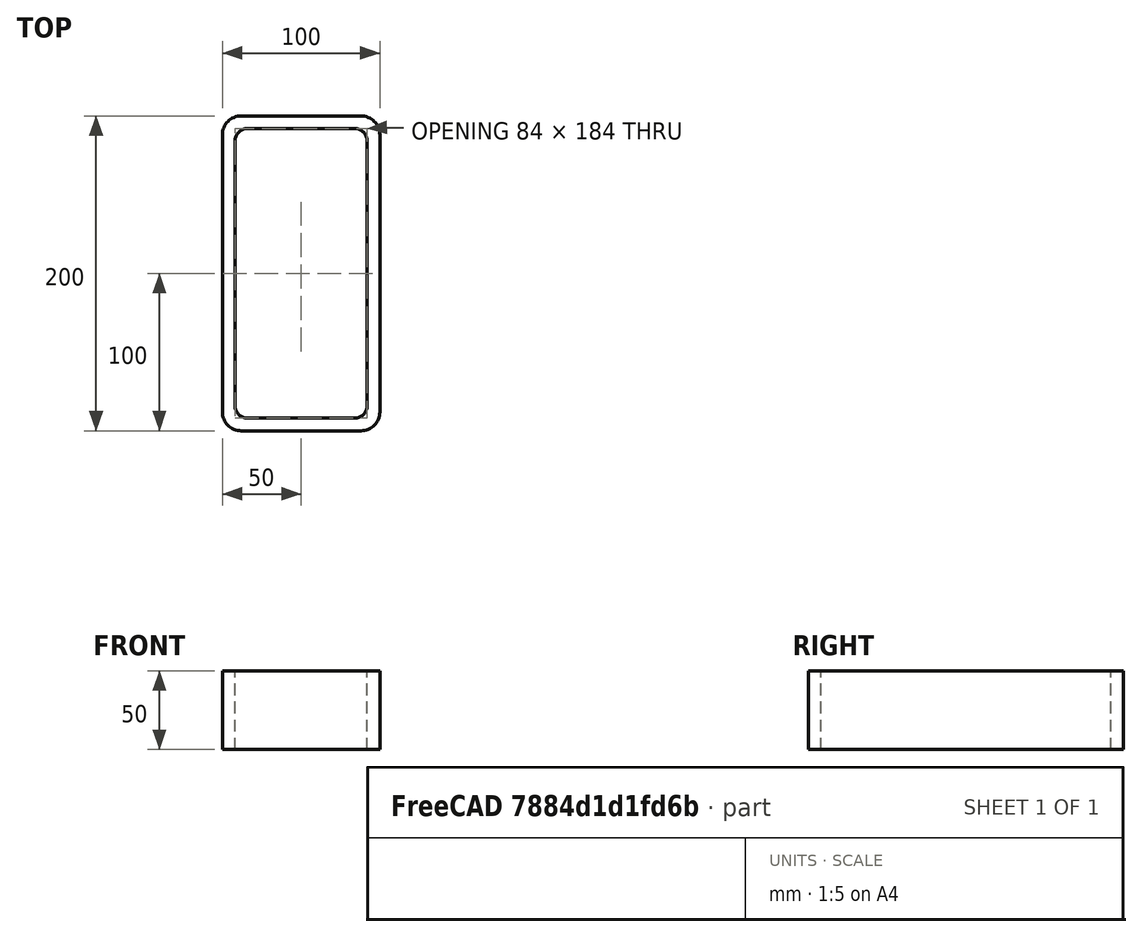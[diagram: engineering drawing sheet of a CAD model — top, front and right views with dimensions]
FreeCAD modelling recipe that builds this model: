
FCSTD DOCUMENT  (FreeCAD 0.15R4671 (Git))
Label: Rectangular hollow section 200x100x8 EN10219 S235JRH
License: All rights reserved
LicenseURL: http://en.wikipedia.org/wiki/All_rights_reserved
objects: Sketcher::SketchObject×1, Part::Extrusion×1
note: 2 computed .brp shape members not serialized (recipe doc carries the construction recipe); baked Part::Feature solids carry a one-line shape summary decoded from their .brp

FEATURE [Sketcher::SketchObject] Sketch
  sketch-geometry (16):
    g0: LineSegment StartX=-34 StartY=92 StartZ=0 EndX=34 EndY=92 EndZ=0
    g1: LineSegment StartX=42 StartY=84 StartZ=0 EndX=42 EndY=-84 EndZ=0
    g2: LineSegment StartX=34 StartY=-92 StartZ=0 EndX=-34 EndY=-92 EndZ=0
    g3: LineSegment StartX=-42 StartY=-84 StartZ=0 EndX=-42 EndY=84 EndZ=0
    g4: LineSegment StartX=-38 StartY=100 StartZ=0 EndX=38 EndY=100 EndZ=0
    g5: LineSegment StartX=50 StartY=88 StartZ=0 EndX=50 EndY=-88 EndZ=0
    g6: LineSegment StartX=38 StartY=-100 StartZ=0 EndX=-38 EndY=-100 EndZ=0
    g7: LineSegment StartX=-50 StartY=-88 StartZ=0 EndX=-50 EndY=88 EndZ=0
    g8: ArcOfCircle CenterX=-34 CenterY=84 CenterZ=0 NormalX=0 NormalY=0 NormalZ=1 Radius=8 StartAngle=1.5708 EndAngle=3.14159
    g9: ArcOfCircle CenterX=34 CenterY=84 CenterZ=0 NormalX=0 NormalY=0 NormalZ=1 Radius=8 StartAngle=0 EndAngle=1.5708
    g10: ArcOfCircle CenterX=34 CenterY=-84 CenterZ=0 NormalX=0 NormalY=0 NormalZ=1 Radius=8 StartAngle=4.71239 EndAngle=6.28319
    g11: ArcOfCircle CenterX=-34 CenterY=-84 CenterZ=0 NormalX=0 NormalY=0 NormalZ=1 Radius=8 StartAngle=3.14159 EndAngle=4.71239
    g12: ArcOfCircle CenterX=38 CenterY=88 CenterZ=0 NormalX=0 NormalY=0 NormalZ=1 Radius=12 StartAngle=0 EndAngle=1.5708
    g13: ArcOfCircle CenterX=38 CenterY=-88 CenterZ=0 NormalX=0 NormalY=0 NormalZ=1 Radius=12 StartAngle=4.71239 EndAngle=6.28319
    g14: ArcOfCircle CenterX=-38 CenterY=-88 CenterZ=0 NormalX=0 NormalY=0 NormalZ=1 Radius=12 StartAngle=3.14159 EndAngle=4.71239
    g15: ArcOfCircle CenterX=-38 CenterY=88 CenterZ=0 NormalX=0 NormalY=0 NormalZ=1 Radius=12 StartAngle=1.5708 EndAngle=3.14159
  constraints (36):
    c: Horizontal(g2)
    c: Vertical(g3)
    c: Horizontal(g6)
    c: Vertical(g7)
    c: Tangent(g3,g8) = 1.5708
    c: Tangent(g0,g8) = 1.5708
    c: Tangent(g0,g9) = 1.5708
    c: Tangent(g1,g9) = 1.5708
    c: Tangent(g1,g10) = 1.5708
    c: Tangent(g2,g10) = 1.5708
    c: Tangent(g2,g11) = 1.5708
    c: Tangent(g3,g11) = 1.5708
    c: Tangent(g4,g12) = 1.5708
    c: Tangent(g5,g12) = 1.5708
    c: Tangent(g5,g13) = 1.5708
    c: Tangent(g6,g13) = 1.5708
    c: Tangent(g6,g14) = 1.5708
    c: Tangent(g7,g14) = 1.5708
    c: Tangent(g7,g15) = 1.5708
    c: Tangent(g4,g15) = 1.5708
    c: Equal(g9,g8)
    c: Equal(g9,g11)
    c: Equal(g9,g10)
    c: Equal(g12,g15)
    c: Equal(g12,g14)
    c: Equal(g12,g13)
    c: Symmetric(g4,g6,g-1)
    c: Symmetric(g7,g5,g-2)
    c: DistanceY(g4,g6) = -200
    c: DistanceX(g7,g5) = 100
    c: Symmetric(g3,g1,g-2)
    c: Symmetric(g0,g2,g-1)
    c: DistanceY(g0,g4) = 8
    c: DistanceX(g5,g1) = -8
    c: Radius(g9) = 8
    c: Radius(g12) = 12
FEATURE [Part::Extrusion] Extrude  label="Rectangular hollow section 200x100x8 EN10219 S235JRH"
  Base = -> Sketch
  Dir = (0,0,50)
  Solid = true
